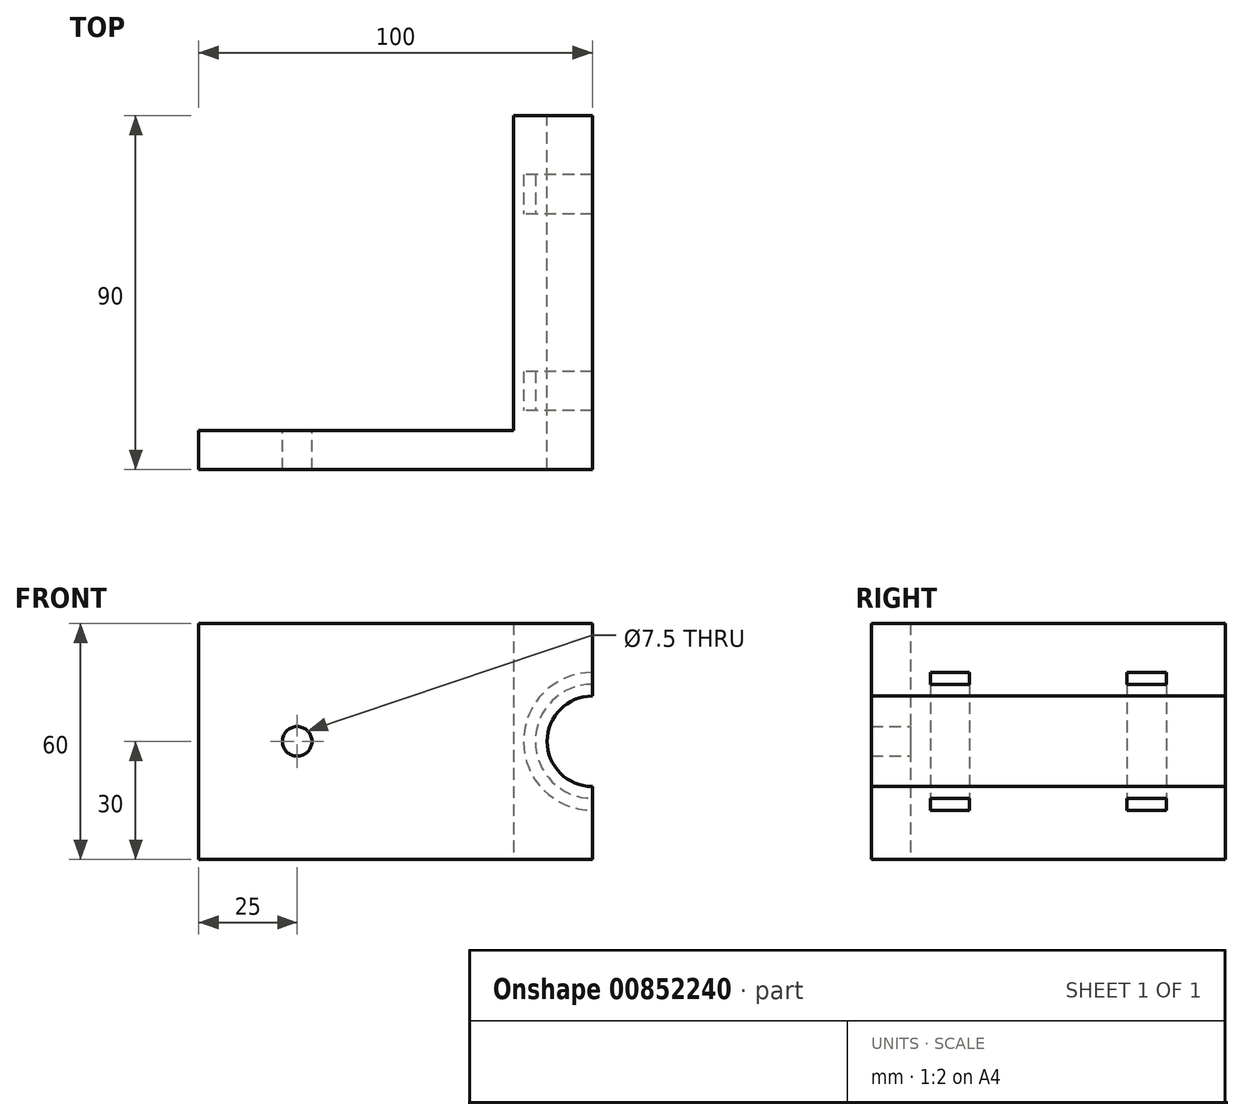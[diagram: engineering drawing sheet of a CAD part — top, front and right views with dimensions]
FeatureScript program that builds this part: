
annotation { "Feature Type Name" : "Feature", "Feature Type Description" : "" }
export const myFeature = defineFeature(function(context is Context, id is Id, definition is map)
    precondition{}
    {
        {
            var Q0;
            Q0=qCreatedBy(makeId("Top.planeOp"),FACE);
            var sketch = newSketch(context, id + "F0", { "sketchPlane" : qUnion([Q0])});
            skLineSegment(sketch, "E0", {"start": v(0, 0) * mm, "end": v(0, 90) * mm});
            skLineSegment(sketch, "E1", {"start": v(0, 90) * mm, "end": v(-20, 90) * mm});
            skLineSegment(sketch, "E2", {"start": v(-20, 90) * mm, "end": v(-20, 10) * mm});
            skLineSegment(sketch, "E3", {"start": v(-20, 10) * mm, "end": v(-100, 10) * mm});
            skLineSegment(sketch, "E4", {"start": v(-100, 10) * mm, "end": v(-100, 0) * mm});
            skLineSegment(sketch, "E5", {"start": v(-100, 0) * mm, "end": v(0, 0) * mm});
            skSolve(sketch);
        }
        {
            var Q0;
            Q0=makeQuery(id+"F0.imprint","IMPRINT",FACE,{"disambiguationData":[TD([[makeQuery(id+"F0.imprint","IMPRINT",EDGE,{"derivedFrom":sQuery(id+"F0.wireOp",EDGE,"E0")}),1.0]])]});
            extrude(context, id + "F1", {"entities" : qUnion([Q0]), "depth" : 60 * mm, "offsetDistance" : 25 * mm});
        }
        {
            var Q0;
            Q0=makeQuery(id+"F1.opExtrude","SWEPT_FACE",FACE,{"disambiguationData":[OSD([sQuery(id+"F0.wireOp",EDGE,"E1")])]});
            var sketch = newSketch(context, id + "F2", { "sketchPlane" : qUnion([Q0])});
            skPoint(sketch, "E6", {"position": v(0, 30) * mm});
            skCircle(sketch, "E7", {"center": v(0, 30) * mm, "radius": 11.5 * mm});
            skSolve(sketch);
        }
        {
            var Q0;
            {var subQ0=sQuery(id+"F2.wireOp",EDGE,"E7");var subQ1=makeQuery(id+"F1.opExtrude","SWEPT_EDGE",EDGE,{"disambiguationData":[OSD([sQuery(id+"F0.wireOp",EDGE,"E0"),sQuery(id+"F0.wireOp",EDGE,"E1")])]});var subQ2=makeQuery(id+"F2.imprint","INTERSECT",VERTEX,{"disambiguationData":[OD(0.0)],"derivedFrom":[subQ1,subQ0]});Q0=makeQuery(id+"F2.imprint","IMPRINT",FACE,{"disambiguationData":[TD([[makeQuery(id+"F2.imprint","IMPRINT",EDGE,{"disambiguationData":[TD([[subQ2,-1.0]])],"derivedFrom":subQ0}),1.0]])]});}
            extrude(context, id + "F3", {"entities" : qUnion([Q0]), "operationType" : NewBodyOperationType.REMOVE, "endBound" : BoundingType.THROUGH_ALL, "oppositeDirection" : true, "depth" : 25 * mm, "offsetDistance" : 25 * mm});
        }
        {
            var Q0;
            Q0=makeQuery(id+"F1.opExtrude","SWEPT_FACE",FACE,{"disambiguationData":[OSD([sQuery(id+"F0.wireOp",EDGE,"E3")])]});
            var sketch = newSketch(context, id + "F4", { "sketchPlane" : qUnion([Q0])});
            skCircle(sketch, "E8", {"center": v(75, 30) * mm, "radius": 3.75 * mm});
            skPoint(sketch, "E8.centerSnap0", {"position": v(100, 30) * mm});
            skSolve(sketch);
        }
        {
            var Q0;
            Q0=makeQuery(id+"F4.imprint","IMPRINT",FACE,{"disambiguationData":[TD([[makeQuery(id+"F4.imprint","IMPRINT",EDGE,{"derivedFrom":sQuery(id+"F4.wireOp",EDGE,"E8")}),1.0]])]});
            extrude(context, id + "F5", {"entities" : qUnion([Q0]), "operationType" : NewBodyOperationType.REMOVE, "endBound" : BoundingType.THROUGH_ALL, "oppositeDirection" : true, "depth" : 25 * mm, "offsetDistance" : 25 * mm});
        }
        {
            var Q0;
            {var subQ0=sQuery(id+"F0.wireOp",EDGE,"E5");var subQ1=sQuery(id+"F0.wireOp",EDGE,"E1");var subQ2=sQuery(id+"F0.wireOp",EDGE,"E0");Q0=makeQuery(id+"F3.boolean.opBoolean","SPLIT",FACE,{"disambiguationData":[TD([makeQuery(id+"F1.opExtrude","CAP_FACE",FACE,{"disambiguationData":[OSD([subQ2,subQ1,sQuery(id+"F0.wireOp",EDGE,"E2"),sQuery(id+"F0.wireOp",EDGE,"E3"),sQuery(id+"F0.wireOp",EDGE,"E4"),subQ0])],"isStart":false})])],"derivedFrom":makeQuery(id+"F1.opExtrude","SWEPT_FACE",FACE,{"disambiguationData":[OSD([subQ2])]})});}
            var sketch = newSketch(context, id + "F6", { "sketchPlane" : qUnion([Q0])});
            skLineSegment(sketch, "E9.bottom", {"start": v(75, 44.5) * mm, "end": v(65, 44.5) * mm});
            skLineSegment(sketch, "E9.top", {"start": v(75, 47.5) * mm, "end": v(65, 47.5) * mm});
            skLineSegment(sketch, "E9.left", {"start": v(75, 44.5) * mm, "end": v(75, 47.5) * mm});
            skLineSegment(sketch, "E9.right", {"start": v(65, 44.5) * mm, "end": v(65, 47.5) * mm});
            skLineSegment(sketch, "E10.bottom", {"start": v(25, 44.5) * mm, "end": v(15, 44.5) * mm});
            skLineSegment(sketch, "E10.top", {"start": v(25, 47.5) * mm, "end": v(15, 47.5) * mm});
            skLineSegment(sketch, "E10.left", {"start": v(25, 44.5) * mm, "end": v(25, 47.5) * mm});
            skLineSegment(sketch, "E10.right", {"start": v(15, 44.5) * mm, "end": v(15, 47.5) * mm});
            skPoint(sketch, "E11", {"position": v(70, 44.5) * mm});
            skLineSegment(sketch, "E12", {"start": v(90, 60) * mm, "end": v(90, 0) * mm, "construction": true});
            skPoint(sketch, "E13", {"position": v(70, 30) * mm});
            skPoint(sketch, "E13.positionSnap0", {"position": v(90, 30) * mm});
            skPoint(sketch, "E14", {"position": v(20, 44.5) * mm});
            skPoint(sketch, "E15", {"position": v(20, 30) * mm});
            skLineSegment(sketch, "E16", {"start": v(90, 30) * mm, "end": v(0, 30) * mm, "construction": true});
            skSolve(sketch);
        }
        {
            var Q0;
            Q0=makeQuery(id+"F6.imprint","IMPRINT",FACE,{"disambiguationData":[TD([[makeQuery(id+"F6.imprint","IMPRINT",EDGE,{"derivedFrom":sQuery(id+"F6.wireOp",EDGE,"E9.bottom")}),-1.0]])]});
            var Q1;
            Q1=makeQuery(id+"F6.imprint","IMPRINT",FACE,{"disambiguationData":[TD([[makeQuery(id+"F6.imprint","IMPRINT",EDGE,{"derivedFrom":sQuery(id+"F6.wireOp",EDGE,"E10.bottom")}),-1.0]])]});
            var Q2;
            Q2=sQuery(id+"F6.wireOp",EDGE,"E16");
            revolve(context, id + "F7", {"operationType" : NewBodyOperationType.REMOVE, "surfaceOperationType" : NewSurfaceOperationType.NEW, "entities" : qUnion([Q0, Q1]), "axis" : qUnion([Q2]), "revolveType" : RevolveType.FULL, "oppositeDirection" : true});
        }
    });
